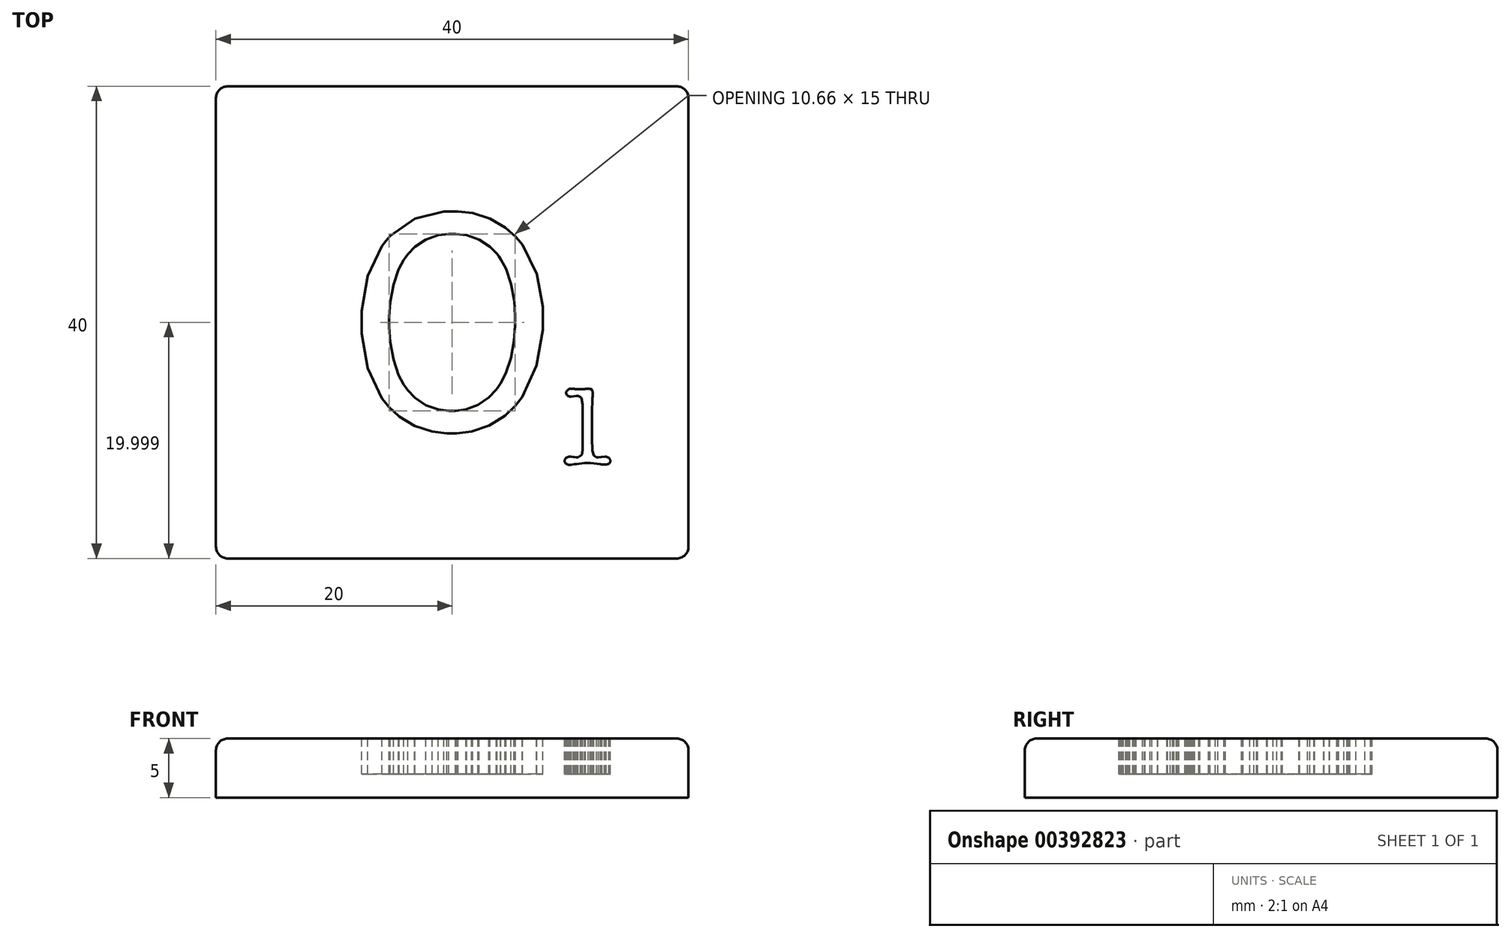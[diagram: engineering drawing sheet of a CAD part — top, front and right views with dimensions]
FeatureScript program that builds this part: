
annotation { "Feature Type Name" : "Feature", "Feature Type Description" : "" }
export const myFeature = defineFeature(function(context is Context, id is Id, definition is map)
    precondition{}
    {
        {
            var Q0;
            Q0=qCreatedBy(makeId("Top.planeOp"),FACE);
            var sketch = newSketch(context, id + "F0", { "sketchPlane" : qUnion([Q0])});
            skLineSegment(sketch, "E0.bottom", {"start": v(20, -20) * mm, "end": v(-20, -20) * mm});
            skLineSegment(sketch, "E0.top", {"start": v(20, 20) * mm, "end": v(-20, 20) * mm});
            skLineSegment(sketch, "E0.left", {"start": v(20, -20) * mm, "end": v(20, 20) * mm});
            skLineSegment(sketch, "E0.right", {"start": v(-20, -20) * mm, "end": v(-20, 20) * mm});
            skPoint(sketch, "E0.middle", {"position": v(0, 0) * mm});
            skSolve(sketch);
        }
        {
            var Q0;
            Q0=makeQuery(id+"F0.imprint","IMPRINT",FACE,{"disambiguationData":[TD([[makeQuery(id+"F0.imprint","IMPRINT",EDGE,{"derivedFrom":sQuery(id+"F0.wireOp",EDGE,"E0.bottom")}),-1.0]])]});
            extrude(context, id + "F1", {"entities" : qUnion([Q0]), "depth" : -5 * mm});
        }
        {
            var Q0;
            Q0=makeQuery(id+"F1.opExtrude","CAP_FACE",FACE,{"disambiguationData":[OSD([sQuery(id+"F0.wireOp",EDGE,"E0.bottom"),sQuery(id+"F0.wireOp",EDGE,"E0.top"),sQuery(id+"F0.wireOp",EDGE,"E0.left"),sQuery(id+"F0.wireOp",EDGE,"E0.right")])],"isStart":true});
            var Q1;
            Q1=makeQuery(id+"F1.opExtrude","SWEPT_EDGE",EDGE,{"disambiguationData":[OSD([sQuery(id+"F0.wireOp",EDGE,"E0.top"),sQuery(id+"F0.wireOp",EDGE,"E0.right")])]});
            var Q2;
            Q2=makeQuery(id+"F1.opExtrude","SWEPT_EDGE",EDGE,{"disambiguationData":[OSD([sQuery(id+"F0.wireOp",EDGE,"E0.top"),sQuery(id+"F0.wireOp",EDGE,"E0.left")])]});
            var Q3;
            Q3=makeQuery(id+"F1.opExtrude","SWEPT_EDGE",EDGE,{"disambiguationData":[OSD([sQuery(id+"F0.wireOp",EDGE,"E0.bottom"),sQuery(id+"F0.wireOp",EDGE,"E0.right")])]});
            var Q4;
            Q4=makeQuery(id+"F1.opExtrude","SWEPT_EDGE",EDGE,{"disambiguationData":[OSD([sQuery(id+"F0.wireOp",EDGE,"E0.bottom"),sQuery(id+"F0.wireOp",EDGE,"E0.left")])]});
            fillet(context, id + "F2", {"entities" : qUnion([Q0, Q1, Q2, Q3, Q4]), "radius" : 1 * mm, "tangentPropagation" : true, "allowEdgeOverflow" : false});
        }
        {
            var Q0;
            Q0=qCreatedBy(makeId("Top.planeOp"),FACE);
            var sketch = newSketch(context, id + "F3", { "sketchPlane" : qUnion([Q0])});
            skLineSegment(sketch, "E1", {"start": v(-0.04, -9.4) * mm, "end": v(-0.46, -9.4) * mm});
            skLineSegment(sketch, "E2", {"start": v(-0.46, -9.4) * mm, "end": v(-1.7, -9.25) * mm});
            skLineSegment(sketch, "E3", {"start": v(-1.7, -9.25) * mm, "end": v(-3.2, -8.77) * mm});
            skLineSegment(sketch, "E4", {"start": v(-3.2, -8.77) * mm, "end": v(-4.5, -7.98) * mm});
            skLineSegment(sketch, "E5", {"start": v(-4.5, -7.98) * mm, "end": v(-5.36, -7.17) * mm});
            skLineSegment(sketch, "E6", {"start": v(-5.36, -7.17) * mm, "end": v(-5.6, -6.87) * mm});
            skLineSegment(sketch, "E7", {"start": v(-5.6, -6.87) * mm, "end": v(-5.95, -6.44) * mm});
            skLineSegment(sketch, "E8", {"start": v(-5.95, -6.44) * mm, "end": v(-7.15, -3.88) * mm});
            skLineSegment(sketch, "E9", {"start": v(-7.15, -3.88) * mm, "end": v(-7.66, -0.96) * mm});
            skLineSegment(sketch, "E10", {"start": v(-7.66, -0.96) * mm, "end": v(-7.66, 0.01) * mm});
            skLineSegment(sketch, "E11", {"start": v(-7.66, 0.01) * mm, "end": v(-7.66, 1) * mm});
            skLineSegment(sketch, "E12", {"start": v(-7.66, 1) * mm, "end": v(-7.14, 3.93) * mm});
            skLineSegment(sketch, "E13", {"start": v(-7.14, 3.93) * mm, "end": v(-5.94, 6.49) * mm});
            skLineSegment(sketch, "E14", {"start": v(-5.94, 6.49) * mm, "end": v(-5.6, 6.9) * mm});
            skLineSegment(sketch, "E15", {"start": v(-5.6, 6.9) * mm, "end": v(-5.25, 7.32) * mm});
            skLineSegment(sketch, "E16", {"start": v(-5.25, 7.32) * mm, "end": v(-3.14, 8.78) * mm});
            skLineSegment(sketch, "E17", {"start": v(-3.14, 8.78) * mm, "end": v(-0.72, 9.4) * mm});
            skLineSegment(sketch, "E18", {"start": v(-0.72, 9.4) * mm, "end": v(0.1, 9.4) * mm});
            skLineSegment(sketch, "E19", {"start": v(0.1, 9.4) * mm, "end": v(0.5, 9.4) * mm});
            skLineSegment(sketch, "E20", {"start": v(0.5, 9.4) * mm, "end": v(1.74, 9.25) * mm});
            skLineSegment(sketch, "E21", {"start": v(1.74, 9.25) * mm, "end": v(3.2, 8.8) * mm});
            skLineSegment(sketch, "E22", {"start": v(3.2, 8.8) * mm, "end": v(4.5, 8.04) * mm});
            skLineSegment(sketch, "E23", {"start": v(4.5, 8.04) * mm, "end": v(5.36, 7.26) * mm});
            skLineSegment(sketch, "E24", {"start": v(5.36, 7.26) * mm, "end": v(5.6, 6.97) * mm});
            skLineSegment(sketch, "E25", {"start": v(5.6, 6.97) * mm, "end": v(5.95, 6.57) * mm});
            skLineSegment(sketch, "E26", {"start": v(5.95, 6.57) * mm, "end": v(7.15, 4.1) * mm});
            skLineSegment(sketch, "E27", {"start": v(7.15, 4.1) * mm, "end": v(7.66, 1.32) * mm});
            skLineSegment(sketch, "E28", {"start": v(7.66, 1.32) * mm, "end": v(7.66, 0.38) * mm});
            skLineSegment(sketch, "E29", {"start": v(7.66, 0.38) * mm, "end": v(7.66, -0.62) * mm});
            skLineSegment(sketch, "E30", {"start": v(7.66, -0.62) * mm, "end": v(7.14, -3.65) * mm});
            skLineSegment(sketch, "E31", {"start": v(7.14, -3.65) * mm, "end": v(5.93, -6.32) * mm});
            skLineSegment(sketch, "E32", {"start": v(5.93, -6.32) * mm, "end": v(5.58, -6.76) * mm});
            skLineSegment(sketch, "E33", {"start": v(5.58, -6.76) * mm, "end": v(5.33, -7.08) * mm});
            skLineSegment(sketch, "E34", {"start": v(5.33, -7.08) * mm, "end": v(4.45, -7.92) * mm});
            skLineSegment(sketch, "E35", {"start": v(4.45, -7.92) * mm, "end": v(3.14, -8.74) * mm});
            skLineSegment(sketch, "E36", {"start": v(3.14, -8.74) * mm, "end": v(1.64, -9.24) * mm});
            skLineSegment(sketch, "E37", {"start": v(1.64, -9.24) * mm, "end": v(0.38, -9.4) * mm});
            skLineSegment(sketch, "E38", {"start": v(0.38, -9.4) * mm, "end": v(-0.04, -9.4) * mm});
            skLineSegment(sketch, "E39", {"start": v(0.01, 7.5) * mm, "end": v(-0.29, 7.5) * mm});
            skLineSegment(sketch, "E40", {"start": v(-0.29, 7.5) * mm, "end": v(-1.19, 7.38) * mm});
            skLineSegment(sketch, "E41", {"start": v(-1.19, 7.38) * mm, "end": v(-2.24, 7.01) * mm});
            skLineSegment(sketch, "E42", {"start": v(-2.24, 7.01) * mm, "end": v(-3.16, 6.4) * mm});
            skLineSegment(sketch, "E43", {"start": v(-3.16, 6.4) * mm, "end": v(-3.76, 5.78) * mm});
            skLineSegment(sketch, "E44", {"start": v(-3.76, 5.78) * mm, "end": v(-3.93, 5.54) * mm});
            skLineSegment(sketch, "E45", {"start": v(-3.93, 5.54) * mm, "end": v(-4.1, 5.3) * mm});
            skLineSegment(sketch, "E46", {"start": v(-4.1, 5.3) * mm, "end": v(-4.54, 4.47) * mm});
            skLineSegment(sketch, "E47", {"start": v(-4.54, 4.47) * mm, "end": v(-4.98, 3.19) * mm});
            skLineSegment(sketch, "E48", {"start": v(-4.98, 3.19) * mm, "end": v(-5.24, 1.71) * mm});
            skLineSegment(sketch, "E49", {"start": v(-5.24, 1.71) * mm, "end": v(-5.33, 0.46) * mm});
            skLineSegment(sketch, "E50", {"start": v(-5.33, 0.46) * mm, "end": v(-5.33, 0.04) * mm});
            skLineSegment(sketch, "E51", {"start": v(-5.33, 0.04) * mm, "end": v(-5.33, -0.38) * mm});
            skLineSegment(sketch, "E52", {"start": v(-5.33, -0.38) * mm, "end": v(-5.24, -1.66) * mm});
            skLineSegment(sketch, "E53", {"start": v(-5.24, -1.66) * mm, "end": v(-4.98, -3.15) * mm});
            skLineSegment(sketch, "E54", {"start": v(-4.98, -3.15) * mm, "end": v(-4.54, -4.44) * mm});
            skLineSegment(sketch, "E55", {"start": v(-4.54, -4.44) * mm, "end": v(-4.1, -5.28) * mm});
            skLineSegment(sketch, "E56", {"start": v(-4.1, -5.28) * mm, "end": v(-3.93, -5.53) * mm});
            skLineSegment(sketch, "E57", {"start": v(-3.93, -5.53) * mm, "end": v(-3.76, -5.76) * mm});
            skLineSegment(sketch, "E58", {"start": v(-3.76, -5.76) * mm, "end": v(-3.16, -6.4) * mm});
            skLineSegment(sketch, "E59", {"start": v(-3.16, -6.4) * mm, "end": v(-2.25, -7) * mm});
            skLineSegment(sketch, "E60", {"start": v(-2.25, -7) * mm, "end": v(-1.2, -7.38) * mm});
            skLineSegment(sketch, "E61", {"start": v(-1.2, -7.38) * mm, "end": v(-0.31, -7.5) * mm});
            skLineSegment(sketch, "E62", {"start": v(-0.31, -7.5) * mm, "end": v(-0.01, -7.5) * mm});
            skLineSegment(sketch, "E63", {"start": v(-0.01, -7.5) * mm, "end": v(0.28, -7.5) * mm});
            skLineSegment(sketch, "E64", {"start": v(0.28, -7.5) * mm, "end": v(1.15, -7.37) * mm});
            skLineSegment(sketch, "E65", {"start": v(1.15, -7.37) * mm, "end": v(2.2, -6.99) * mm});
            skLineSegment(sketch, "E66", {"start": v(2.2, -6.99) * mm, "end": v(3.1, -6.35) * mm});
            skLineSegment(sketch, "E67", {"start": v(3.1, -6.35) * mm, "end": v(3.72, -5.7) * mm});
            skLineSegment(sketch, "E68", {"start": v(3.72, -5.7) * mm, "end": v(3.89, -5.45) * mm});
            skLineSegment(sketch, "E69", {"start": v(3.89, -5.45) * mm, "end": v(4.07, -5.19) * mm});
            skLineSegment(sketch, "E70", {"start": v(4.07, -5.19) * mm, "end": v(4.52, -4.33) * mm});
            skLineSegment(sketch, "E71", {"start": v(4.52, -4.33) * mm, "end": v(4.97, -3.03) * mm});
            skLineSegment(sketch, "E72", {"start": v(4.97, -3.03) * mm, "end": v(5.24, -1.55) * mm});
            skLineSegment(sketch, "E73", {"start": v(5.24, -1.55) * mm, "end": v(5.33, -0.3) * mm});
            skLineSegment(sketch, "E74", {"start": v(5.33, -0.3) * mm, "end": v(5.33, 0.12) * mm});
            skLineSegment(sketch, "E75", {"start": v(5.33, 0.12) * mm, "end": v(5.33, 0.54) * mm});
            skLineSegment(sketch, "E76", {"start": v(5.33, 0.54) * mm, "end": v(5.24, 1.8) * mm});
            skLineSegment(sketch, "E77", {"start": v(5.24, 1.8) * mm, "end": v(4.99, 3.26) * mm});
            skLineSegment(sketch, "E78", {"start": v(4.99, 3.26) * mm, "end": v(4.56, 4.52) * mm});
            skLineSegment(sketch, "E79", {"start": v(4.56, 4.52) * mm, "end": v(4.13, 5.34) * mm});
            skLineSegment(sketch, "E80", {"start": v(4.13, 5.34) * mm, "end": v(3.95, 5.58) * mm});
            skLineSegment(sketch, "E81", {"start": v(3.95, 5.58) * mm, "end": v(3.8, 5.81) * mm});
            skLineSegment(sketch, "E82", {"start": v(3.8, 5.81) * mm, "end": v(3.2, 6.42) * mm});
            skLineSegment(sketch, "E83", {"start": v(3.2, 6.42) * mm, "end": v(2.28, 7.02) * mm});
            skLineSegment(sketch, "E84", {"start": v(2.28, 7.02) * mm, "end": v(1.22, 7.38) * mm});
            skLineSegment(sketch, "E85", {"start": v(1.22, 7.38) * mm, "end": v(0.32, 7.5) * mm});
            skLineSegment(sketch, "E86", {"start": v(0.32, 7.5) * mm, "end": v(0.01, 7.5) * mm});
            skSolve(sketch);
        }
        {
            var Q0;
            Q0=qCreatedBy(makeId("Top.planeOp"),FACE);
            var sketch = newSketch(context, id + "F4", { "sketchPlane" : qUnion([Q0])});
            skLineSegment(sketch, "E87", {"start": v(11.05, -9.8) * mm, "end": v(11.02, -7.04) * mm});
            skLineSegment(sketch, "E88", {"start": v(11.02, -7.04) * mm, "end": v(11.02, -6.96) * mm});
            skLineSegment(sketch, "E89", {"start": v(11.02, -6.96) * mm, "end": v(10.94, -6.42) * mm});
            skLineSegment(sketch, "E90", {"start": v(10.94, -6.42) * mm, "end": v(10.92, -6.4) * mm});
            skLineSegment(sketch, "E91", {"start": v(10.92, -6.4) * mm, "end": v(10.9, -6.37) * mm});
            skLineSegment(sketch, "E92", {"start": v(10.9, -6.37) * mm, "end": v(10.65, -6.23) * mm});
            skLineSegment(sketch, "E93", {"start": v(10.65, -6.23) * mm, "end": v(10.57, -6.23) * mm});
            skLineSegment(sketch, "E94", {"start": v(10.57, -6.23) * mm, "end": v(10.5, -6.23) * mm});
            skLineSegment(sketch, "E95", {"start": v(10.5, -6.23) * mm, "end": v(10.32, -6.25) * mm});
            skLineSegment(sketch, "E96", {"start": v(10.32, -6.25) * mm, "end": v(10.29, -6.26) * mm});
            skLineSegment(sketch, "E97", {"start": v(10.29, -6.26) * mm, "end": v(10.26, -6.26) * mm});
            skLineSegment(sketch, "E98", {"start": v(10.26, -6.26) * mm, "end": v(10.07, -6.28) * mm});
            skLineSegment(sketch, "E99", {"start": v(10.07, -6.28) * mm, "end": v(10.01, -6.28) * mm});
            skLineSegment(sketch, "E100", {"start": v(10.01, -6.28) * mm, "end": v(9.94, -6.28) * mm});
            skLineSegment(sketch, "E101", {"start": v(9.94, -6.28) * mm, "end": v(9.73, -6.2) * mm});
            skLineSegment(sketch, "E102", {"start": v(9.73, -6.2) * mm, "end": v(9.64, -6.01) * mm});
            skLineSegment(sketch, "E103", {"start": v(9.64, -6.01) * mm, "end": v(9.64, -5.95) * mm});
            skLineSegment(sketch, "E104", {"start": v(9.64, -5.95) * mm, "end": v(9.64, -5.86) * mm});
            skLineSegment(sketch, "E105", {"start": v(9.64, -5.86) * mm, "end": v(9.9, -5.61) * mm});
            skLineSegment(sketch, "E106", {"start": v(9.9, -5.61) * mm, "end": v(10, -5.61) * mm});
            skLineSegment(sketch, "E107", {"start": v(10, -5.61) * mm, "end": v(10.08, -5.61) * mm});
            skLineSegment(sketch, "E108", {"start": v(10.08, -5.61) * mm, "end": v(10.31, -5.63) * mm});
            skLineSegment(sketch, "E109", {"start": v(10.31, -5.63) * mm, "end": v(10.35, -5.64) * mm});
            skLineSegment(sketch, "E110", {"start": v(10.35, -5.64) * mm, "end": v(10.4, -5.64) * mm});
            skLineSegment(sketch, "E111", {"start": v(10.4, -5.64) * mm, "end": v(10.64, -5.66) * mm});
            skLineSegment(sketch, "E112", {"start": v(10.64, -5.66) * mm, "end": v(10.73, -5.66) * mm});
            skLineSegment(sketch, "E113", {"start": v(10.73, -5.66) * mm, "end": v(10.85, -5.66) * mm});
            skLineSegment(sketch, "E114", {"start": v(10.85, -5.66) * mm, "end": v(11.2, -5.65) * mm});
            skLineSegment(sketch, "E115", {"start": v(11.2, -5.65) * mm, "end": v(11.23, -5.64) * mm});
            skLineSegment(sketch, "E116", {"start": v(11.23, -5.64) * mm, "end": v(11.28, -5.64) * mm});
            skLineSegment(sketch, "E117", {"start": v(11.28, -5.64) * mm, "end": v(11.52, -5.61) * mm});
            skLineSegment(sketch, "E118", {"start": v(11.52, -5.61) * mm, "end": v(11.6, -5.61) * mm});
            skLineSegment(sketch, "E119", {"start": v(11.6, -5.61) * mm, "end": v(11.66, -5.61) * mm});
            skLineSegment(sketch, "E120", {"start": v(11.66, -5.61) * mm, "end": v(11.84, -5.72) * mm});
            skLineSegment(sketch, "E121", {"start": v(11.84, -5.72) * mm, "end": v(11.85, -5.74) * mm});
            skLineSegment(sketch, "E122", {"start": v(11.85, -5.74) * mm, "end": v(11.86, -5.75) * mm});
            skLineSegment(sketch, "E123", {"start": v(11.86, -5.75) * mm, "end": v(11.89, -5.96) * mm});
            skLineSegment(sketch, "E124", {"start": v(11.89, -5.96) * mm, "end": v(11.89, -6.03) * mm});
            skLineSegment(sketch, "E125", {"start": v(11.89, -6.03) * mm, "end": v(11.89, -6.1) * mm});
            skLineSegment(sketch, "E126", {"start": v(11.89, -6.1) * mm, "end": v(11.88, -6.23) * mm});
            skLineSegment(sketch, "E127", {"start": v(11.88, -6.23) * mm, "end": v(11.88, -6.26) * mm});
            skLineSegment(sketch, "E128", {"start": v(11.88, -6.26) * mm, "end": v(11.87, -6.43) * mm});
            skLineSegment(sketch, "E129", {"start": v(11.87, -6.43) * mm, "end": v(11.83, -7.69) * mm});
            skLineSegment(sketch, "E130", {"start": v(11.83, -7.69) * mm, "end": v(11.83, -8.11) * mm});
            skLineSegment(sketch, "E131", {"start": v(11.83, -8.11) * mm, "end": v(11.83, -9.19) * mm});
            skLineSegment(sketch, "E132", {"start": v(11.83, -9.19) * mm, "end": v(11.84, -9.9) * mm});
            skLineSegment(sketch, "E133", {"start": v(11.84, -9.9) * mm, "end": v(11.84, -9.98) * mm});
            skLineSegment(sketch, "E134", {"start": v(11.84, -9.98) * mm, "end": v(11.85, -10.08) * mm});
            skLineSegment(sketch, "E135", {"start": v(11.85, -10.08) * mm, "end": v(11.86, -10.6) * mm});
            skLineSegment(sketch, "E136", {"start": v(11.86, -10.6) * mm, "end": v(11.86, -10.77) * mm});
            skLineSegment(sketch, "E137", {"start": v(11.86, -10.77) * mm, "end": v(11.86, -10.88) * mm});
            skLineSegment(sketch, "E138", {"start": v(11.86, -10.88) * mm, "end": v(11.98, -11.26) * mm});
            skLineSegment(sketch, "E139", {"start": v(11.98, -11.26) * mm, "end": v(12.22, -11.42) * mm});
            skLineSegment(sketch, "E140", {"start": v(12.22, -11.42) * mm, "end": v(12.3, -11.42) * mm});
            skLineSegment(sketch, "E141", {"start": v(12.3, -11.42) * mm, "end": v(12.38, -11.42) * mm});
            skLineSegment(sketch, "E142", {"start": v(12.38, -11.42) * mm, "end": v(12.58, -11.4) * mm});
            skLineSegment(sketch, "E143", {"start": v(12.58, -11.4) * mm, "end": v(12.61, -11.4) * mm});
            skLineSegment(sketch, "E144", {"start": v(12.61, -11.4) * mm, "end": v(12.65, -11.4) * mm});
            skLineSegment(sketch, "E145", {"start": v(12.65, -11.4) * mm, "end": v(12.93, -11.38) * mm});
            skLineSegment(sketch, "E146", {"start": v(12.93, -11.38) * mm, "end": v(13.01, -11.38) * mm});
            skLineSegment(sketch, "E147", {"start": v(13.01, -11.38) * mm, "end": v(13.27, -11.46) * mm});
            skLineSegment(sketch, "E148", {"start": v(13.27, -11.46) * mm, "end": v(13.39, -11.65) * mm});
            skLineSegment(sketch, "E149", {"start": v(13.39, -11.65) * mm, "end": v(13.39, -11.71) * mm});
            skLineSegment(sketch, "E150", {"start": v(13.39, -11.71) * mm, "end": v(13.39, -11.77) * mm});
            skLineSegment(sketch, "E151", {"start": v(13.39, -11.77) * mm, "end": v(13.28, -11.96) * mm});
            skLineSegment(sketch, "E152", {"start": v(13.28, -11.96) * mm, "end": v(13.04, -12.04) * mm});
            skLineSegment(sketch, "E153", {"start": v(13.04, -12.04) * mm, "end": v(12.97, -12.04) * mm});
            skLineSegment(sketch, "E154", {"start": v(12.97, -12.04) * mm, "end": v(12.89, -12.04) * mm});
            skLineSegment(sketch, "E155", {"start": v(12.89, -12.04) * mm, "end": v(12.68, -12.03) * mm});
            skLineSegment(sketch, "E156", {"start": v(12.68, -12.03) * mm, "end": v(12.66, -12.03) * mm});
            skLineSegment(sketch, "E157", {"start": v(12.66, -12.03) * mm, "end": v(12.53, -12) * mm});
            skLineSegment(sketch, "E158", {"start": v(12.53, -12) * mm, "end": v(11.71, -11.92) * mm});
            skLineSegment(sketch, "E159", {"start": v(11.71, -11.92) * mm, "end": v(11.44, -11.92) * mm});
            skLineSegment(sketch, "E160", {"start": v(11.44, -11.92) * mm, "end": v(11.18, -11.92) * mm});
            skLineSegment(sketch, "E161", {"start": v(11.18, -11.92) * mm, "end": v(10.51, -12) * mm});
            skLineSegment(sketch, "E162", {"start": v(10.51, -12) * mm, "end": v(10.41, -12) * mm});
            skLineSegment(sketch, "E163", {"start": v(10.41, -12) * mm, "end": v(10.36, -12.01) * mm});
            skLineSegment(sketch, "E164", {"start": v(10.36, -12.01) * mm, "end": v(10.03, -12.05) * mm});
            skLineSegment(sketch, "E165", {"start": v(10.03, -12.05) * mm, "end": v(9.93, -12.05) * mm});
            skLineSegment(sketch, "E166", {"start": v(9.93, -12.05) * mm, "end": v(9.85, -12.05) * mm});
            skLineSegment(sketch, "E167", {"start": v(9.85, -12.05) * mm, "end": v(9.62, -11.97) * mm});
            skLineSegment(sketch, "E168", {"start": v(9.62, -11.97) * mm, "end": v(9.52, -11.77) * mm});
            skLineSegment(sketch, "E169", {"start": v(9.52, -11.77) * mm, "end": v(9.52, -11.71) * mm});
            skLineSegment(sketch, "E170", {"start": v(9.52, -11.71) * mm, "end": v(9.52, -11.65) * mm});
            skLineSegment(sketch, "E171", {"start": v(9.52, -11.65) * mm, "end": v(9.63, -11.46) * mm});
            skLineSegment(sketch, "E172", {"start": v(9.63, -11.46) * mm, "end": v(9.9, -11.38) * mm});
            skLineSegment(sketch, "E173", {"start": v(9.9, -11.38) * mm, "end": v(9.99, -11.38) * mm});
            skLineSegment(sketch, "E174", {"start": v(9.99, -11.38) * mm, "end": v(10.06, -11.38) * mm});
            skLineSegment(sketch, "E175", {"start": v(10.06, -11.38) * mm, "end": v(10.25, -11.4) * mm});
            skLineSegment(sketch, "E176", {"start": v(10.25, -11.4) * mm, "end": v(10.28, -11.4) * mm});
            skLineSegment(sketch, "E177", {"start": v(10.28, -11.4) * mm, "end": v(10.32, -11.4) * mm});
            skLineSegment(sketch, "E178", {"start": v(10.32, -11.4) * mm, "end": v(10.5, -11.42) * mm});
            skLineSegment(sketch, "E179", {"start": v(10.5, -11.42) * mm, "end": v(10.57, -11.42) * mm});
            skLineSegment(sketch, "E180", {"start": v(10.57, -11.42) * mm, "end": v(10.67, -11.42) * mm});
            skLineSegment(sketch, "E181", {"start": v(10.67, -11.42) * mm, "end": v(10.96, -11.2) * mm});
            skLineSegment(sketch, "E182", {"start": v(10.96, -11.2) * mm, "end": v(10.98, -11.16) * mm});
            skLineSegment(sketch, "E183", {"start": v(10.98, -11.16) * mm, "end": v(10.99, -11.12) * mm});
            skLineSegment(sketch, "E184", {"start": v(10.99, -11.12) * mm, "end": v(11.03, -10.7) * mm});
            skLineSegment(sketch, "E185", {"start": v(11.03, -10.7) * mm, "end": v(11.05, -10.03) * mm});
            skLineSegment(sketch, "E186", {"start": v(11.05, -10.03) * mm, "end": v(11.05, -9.8) * mm});
            skSolve(sketch);
        }
        {
            var Q0;
            Q0=qSketchRegion(id+"F3",true);
            var Q1;
            Q1=qSketchRegion(id+"F4",true);
            extrude(context, id + "F5", {"entities" : qUnion([Q0, Q1]), "depth" : -3 * mm});
        }
    });
